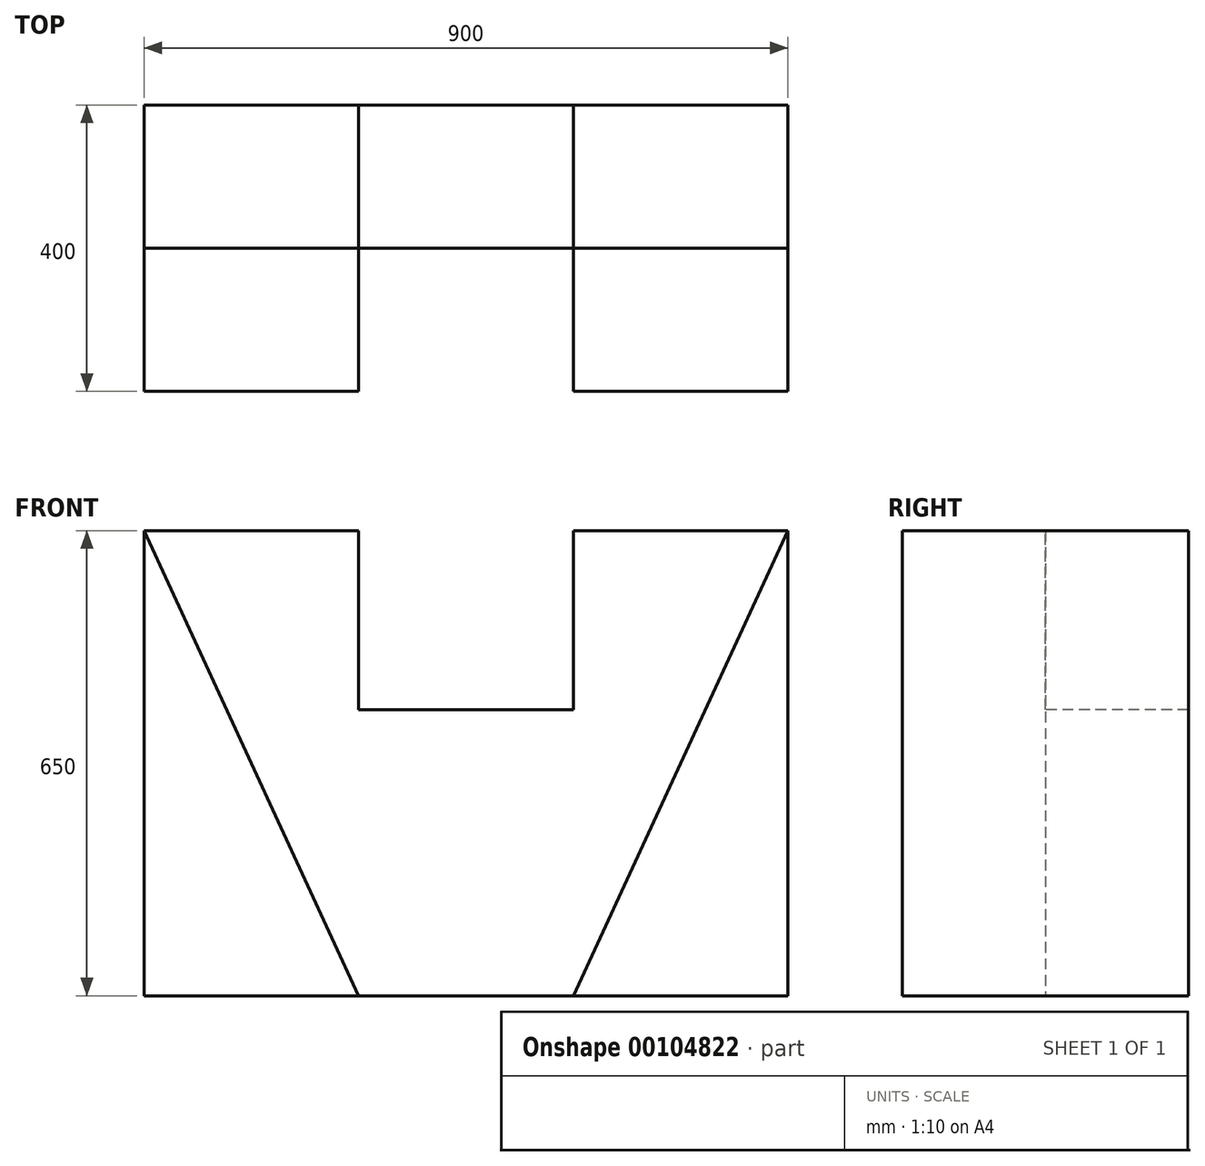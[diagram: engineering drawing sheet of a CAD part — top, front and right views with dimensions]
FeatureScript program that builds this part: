
annotation { "Feature Type Name" : "Feature", "Feature Type Description" : "" }
export const myFeature = defineFeature(function(context is Context, id is Id, definition is map)
    precondition{}
    {
        {
            var Q0;
            Q0=qCreatedBy(makeId("Front.planeOp"),FACE);
            var sketch = newSketch(context, id + "F0", { "sketchPlane" : qUnion([Q0])});
            skLineSegment(sketch, "E0.bottom", {"start": v(450, 325) * mm, "end": v(-450, 325) * mm});
            skLineSegment(sketch, "E0.top", {"start": v(450, -325) * mm, "end": v(-450, -325) * mm});
            skLineSegment(sketch, "E0.left", {"start": v(450, 325) * mm, "end": v(450, -325) * mm});
            skLineSegment(sketch, "E0.right", {"start": v(-450, 325) * mm, "end": v(-450, -325) * mm});
            skPoint(sketch, "E0.middle", {"position": v(0, 0) * mm});
            skSolve(sketch);
        }
        {
            var Q0;
            Q0 = qSketchRegion(id + "F0", true);
            extrude(context, id + "F1", {"entities" : qUnion([Q0]), "depth" : 200 * mm});
        }
        {
            var Q0;
            Q0=makeQuery(id+"F1.opExtrude","CAP_FACE",FACE,{"disambiguationData":[OSD([sQuery(id+"F0.wireOp",EDGE,"E0.bottom"),sQuery(id+"F0.wireOp",EDGE,"E0.top"),sQuery(id+"F0.wireOp",EDGE,"E0.left"),sQuery(id+"F0.wireOp",EDGE,"E0.right")])],"isStart":false});
            var sketch = newSketch(context, id + "F2", { "sketchPlane" : qUnion([Q0])});
            skLineSegment(sketch, "E1.bottom", {"start": v(150, 75) * mm, "end": v(-150, 75) * mm});
            skLineSegment(sketch, "E1.top", {"start": v(150, 575) * mm, "end": v(-150, 575) * mm});
            skLineSegment(sketch, "E1.left", {"start": v(150, 75) * mm, "end": v(150, 575) * mm});
            skLineSegment(sketch, "E1.right", {"start": v(-150, 75) * mm, "end": v(-150, 575) * mm});
            skPoint(sketch, "E1.middle", {"position": v(0, 325) * mm});
            skSolve(sketch);
        }
        {
            var Q0;
            Q0 = qSketchRegion(id + "F2", true);
            extrude(context, id + "F3", {"entities" : qUnion([Q0]), "operationType" : NewBodyOperationType.REMOVE, "endBound" : BoundingType.THROUGH_ALL, "oppositeDirection" : true, "depth" : 25 * mm});
        }
        {
            var Q0;
            Q0=makeQuery(id+"F1.opExtrude","CAP_FACE",FACE,{"disambiguationData":[OSD([sQuery(id+"F0.wireOp",EDGE,"E0.bottom"),sQuery(id+"F0.wireOp",EDGE,"E0.top"),sQuery(id+"F0.wireOp",EDGE,"E0.left"),sQuery(id+"F0.wireOp",EDGE,"E0.right")])],"isStart":false});
            var sketch = newSketch(context, id + "F4", { "sketchPlane" : qUnion([Q0])});
            skLineSegment(sketch, "E2", {"start": v(-450, 325) * mm, "end": v(-150, -325) * mm});
            skLineSegment(sketch, "E3", {"start": v(450, 325) * mm, "end": v(150, -325) * mm});
            skLineSegment(sketch, "E4", {"start": v(-450, 325) * mm, "end": v(-450, -325) * mm});
            skLineSegment(sketch, "E5", {"start": v(-450, -325) * mm, "end": v(-150, -325) * mm});
            skLineSegment(sketch, "E6", {"start": v(450, 325) * mm, "end": v(450, -325) * mm});
            skLineSegment(sketch, "E7", {"start": v(450, -325) * mm, "end": v(150, -325) * mm});
            skSolve(sketch);
        }
        {
            var Q0;
            Q0 = qSketchRegion(id + "F4", true);
            extrude(context, id + "F5", {"entities" : qUnion([Q0]), "operationType" : NewBodyOperationType.ADD, "depth" : 200 * mm});
        }
    });
